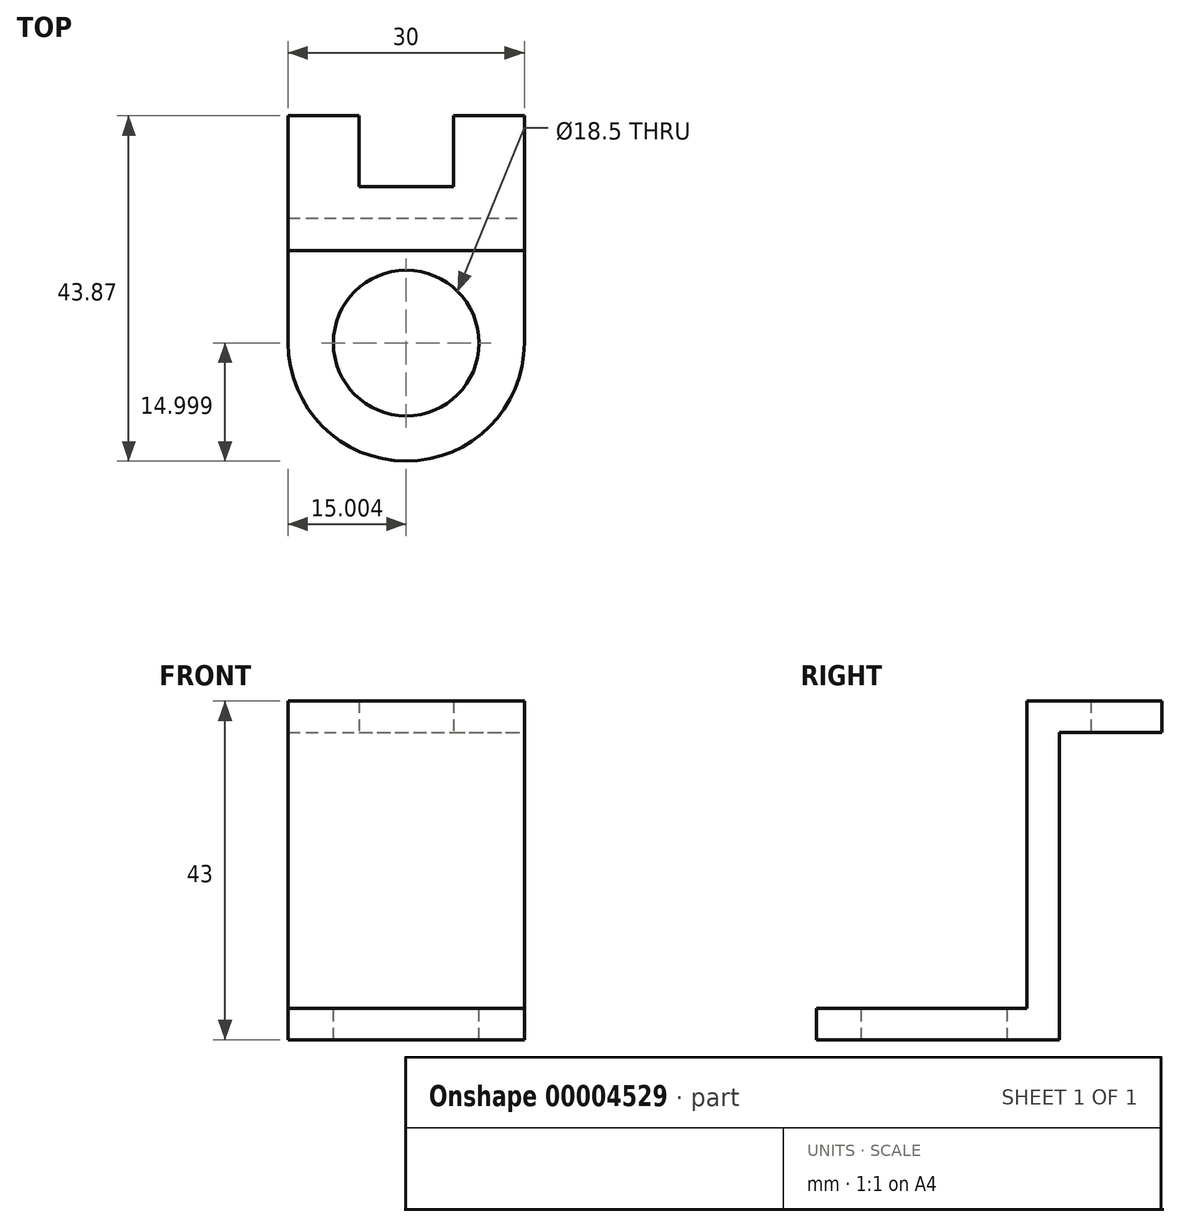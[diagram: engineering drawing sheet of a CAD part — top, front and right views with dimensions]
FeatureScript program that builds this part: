
annotation { "Feature Type Name" : "Feature", "Feature Type Description" : "" }
export const myFeature = defineFeature(function(context is Context, id is Id, definition is map)
    precondition{}
    {
        {
            var Q0;
            Q0=qCreatedBy(makeId("Top.planeOp"),FACE);
            var sketch = newSketch(context, id + "F0", { "sketchPlane" : qUnion([Q0])});
            skLineSegment(sketch, "E0.top", {"start": v(-16.68, 9) * mm, "end": v(-7.68, 9) * mm});
            skLineSegment(sketch, "E0.left", {"start": v(-16.68, 0) * mm, "end": v(-16.68, 9) * mm});
            skLineSegment(sketch, "E0.right", {"start": v(-7.68, 0) * mm, "end": v(-7.68, 9) * mm});
            skLineSegment(sketch, "E1.top", {"start": v(4.32, 9) * mm, "end": v(13.32, 9) * mm});
            skLineSegment(sketch, "E1.left", {"start": v(4.32, 0) * mm, "end": v(4.32, 9) * mm});
            skLineSegment(sketch, "E1.right", {"start": v(13.32, 0) * mm, "end": v(13.32, 9) * mm});
            skCircle(sketch, "E2", {"center": v(-1.68, -19.87) * mm, "radius": 9.25 * mm});
            skArc(sketch, "E3", {"start": v(-16.68, -19.87) * mm, "mid": v(-12.28, -30.48) * mm, "end": v(-1.68, -34.87) * mm});
            skLineSegment(sketch, "E4", {"start": v(-16.68, 0) * mm, "end": v(-16.68, -19.87) * mm});
            skLineSegment(sketch, "E5", {"start": v(-1.68, -34.87) * mm, "end": v(-1.68, 0) * mm, "construction": true});
            skLineSegment(sketch, "E6.0.MirrorCS", {"start": v(13.32, 0) * mm, "end": v(13.32, -19.87) * mm});
            skArc(sketch, "E7.0.MirrorCS", {"start": v(13.32, -19.87) * mm, "mid": v(8.93, -30.48) * mm, "end": v(-1.68, -34.87) * mm});
            skLineSegment(sketch, "E8", {"start": v(-7.68, 0) * mm, "end": v(4.32, 0) * mm});
            skLineSegment(sketch, "E9", {"start": v(13.32, -8.13) * mm, "end": v(-16.68, -8.13) * mm});
            skLineSegment(sketch, "E10", {"start": v(-16.68, -4.02) * mm, "end": v(13.32, -4.02) * mm});
            skSolve(sketch);
        }
        {
            var Q0;
            Q0=makeQuery(id+"F0.imprint","IMPRINT",FACE,{"disambiguationData":[TD([[makeQuery(id+"F0.imprint","IMPRINT",EDGE,{"derivedFrom":sQuery(id+"F0.wireOp",EDGE,"E0.top")}),-1.0]])]});
            var Q1;
            {var subQ1=sQuery(id+"F0.wireOp",EDGE,"E9");Q1=makeQuery(id+"F0.imprint","IMPRINT",FACE,{"disambiguationData":[TD([[makeQuery(id+"F0.imprint","IMPRINT",EDGE,{"derivedFrom":subQ1}),-1.0]])]});}
            extrude(context, id + "F1", {"entities" : qUnion([Q0, Q1]), "depth" : 4 * mm});
        }
        {
            var Q0;
            {var subQ1=sQuery(id+"F0.wireOp",EDGE,"E9");Q0=makeQuery(id+"F0.imprint","IMPRINT",FACE,{"disambiguationData":[TD([[makeQuery(id+"F0.imprint","IMPRINT",EDGE,{"derivedFrom":subQ1}),-1.0]])]});}
            extrude(context, id + "F2", {"entities" : qUnion([Q0]), "operationType" : NewBodyOperationType.ADD, "oppositeDirection" : true, "depth" : 35 * mm});
        }
        {
            var Q0;
            Q0=makeQuery(id+"F2.opExtrude","CAP_FACE",FACE,{"disambiguationData":[OSD([sQuery(id+"F0.wireOp",EDGE,"E4"),sQuery(id+"F0.wireOp",EDGE,"E6.0.MirrorCS"),sQuery(id+"F0.wireOp",EDGE,"E9"),sQuery(id+"F0.wireOp",EDGE,"E10")])],"isStart":false});
            var sketch = newSketch(context, id + "F3", { "sketchPlane" : qUnion([Q0])});
            skLineSegment(sketch, "E11.1.0", {"start": v(-16.68, 8.13) * mm, "end": v(-16.68, 19.87) * mm});
            skArc(sketch, "E11.1.1", {"start": v(-16.68, 19.87) * mm, "mid": v(-1.68, 34.87) * mm, "end": v(13.32, 19.87) * mm});
            skLineSegment(sketch, "E11.1.2", {"start": v(13.32, 8.13) * mm, "end": v(13.32, 19.87) * mm});
            skLineSegment(sketch, "E11.1.3", {"start": v(13.32, 8.13) * mm, "end": v(-16.68, 8.13) * mm});
            skCircle(sketch, "E12.2", {"center": v(-1.68, 19.87) * mm, "radius": 9.25 * mm});
            skSolve(sketch);
        }
        {
            var Q0;
            Q0=makeQuery(id+"F3.imprint","IMPRINT",FACE,{"disambiguationData":[TD([[makeQuery(id+"F3.imprint","IMPRINT",EDGE,{"derivedFrom":sQuery(id+"F3.wireOp",EDGE,"E11.1.0")}),-1.0]])]});
            var Q1;
            Q1=makeQuery(id+"F3.imprint","IMPRINT",FACE,{"disambiguationData":[TD([[makeQuery(id+"F3.imprint","IMPRINT",EDGE,{"derivedFrom":sQuery(id+"F3.wireOp",EDGE,"E11.1.0")}),-1.0]])]});
            var Q2;
            Q2=makeQuery(id+"F3.imprint","IMPRINT",FACE,{"disambiguationData":[TD([[makeQuery(id+"F3.imprint","IMPRINT",EDGE,{"derivedFrom":sQuery(id+"F3.wireOp",EDGE,"E11.1.3")}),1.0]])]});
            extrude(context, id + "F4", {"entities" : qUnion([Q0, Q1, Q2]), "operationType" : NewBodyOperationType.ADD, "depth" : 4 * mm});
        }
    });
